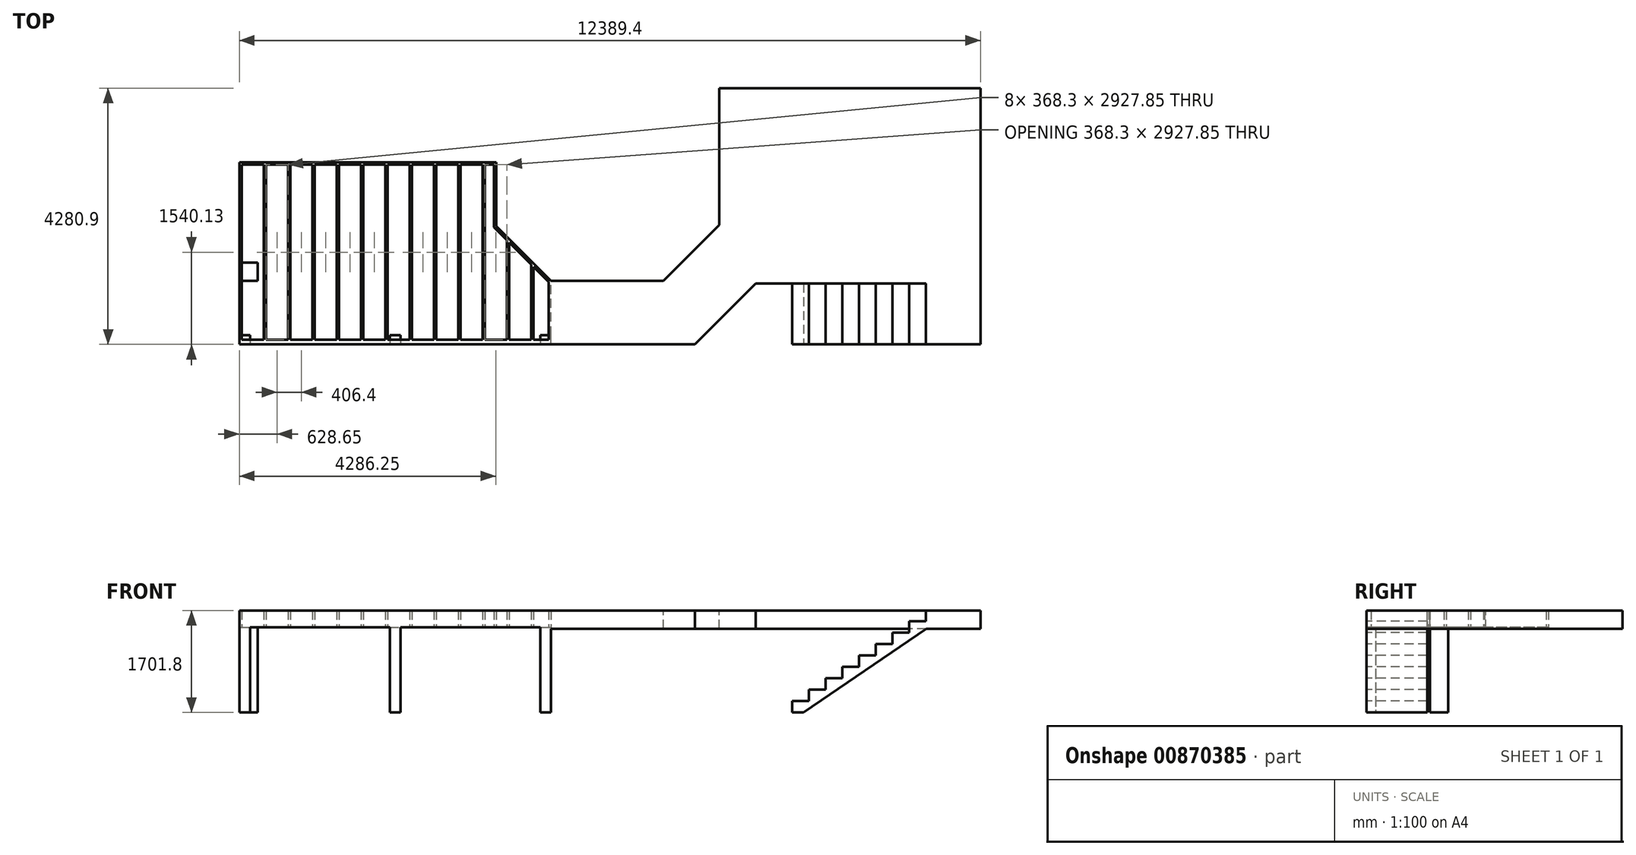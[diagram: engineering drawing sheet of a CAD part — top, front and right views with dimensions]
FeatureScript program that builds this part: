
annotation { "Feature Type Name" : "Feature", "Feature Type Description" : "" }
export const myFeature = defineFeature(function(context is Context, id is Id, definition is map)
    precondition{}
    {
        {
            var Q0;
            Q0=qCreatedBy(makeId("Top.planeOp"),FACE);
            var sketch = newSketch(context, id + "F0", { "sketchPlane" : qUnion([Q0])});
            skLineSegment(sketch, "E0.bottom", {"start": v(0, -1676.4) * mm, "end": v(304.8, -1676.4) * mm});
            skLineSegment(sketch, "E0.top", {"start": v(0, -1981.2) * mm, "end": v(304.8, -1981.2) * mm});
            skLineSegment(sketch, "E0.left", {"start": v(0, -1676.4) * mm, "end": v(0, -1981.2) * mm});
            skLineSegment(sketch, "E0.right", {"start": v(304.8, -1676.4) * mm, "end": v(304.8, -1981.2) * mm});
            skLineSegment(sketch, "E1.bottom", {"start": v(0, -2889.75) * mm, "end": v(177.8, -2889.75) * mm});
            skLineSegment(sketch, "E1.top", {"start": v(0, -3042.15) * mm, "end": v(177.8, -3042.15) * mm});
            skLineSegment(sketch, "E1.left", {"start": v(0, -2889.75) * mm, "end": v(0, -3042.15) * mm});
            skLineSegment(sketch, "E1.right", {"start": v(177.8, -2889.75) * mm, "end": v(177.8, -3042.15) * mm});
            skLineSegment(sketch, "E2.bottom", {"start": v(2514.6, -2889.75) * mm, "end": v(2692.4, -2889.75) * mm});
            skLineSegment(sketch, "E2.top", {"start": v(2514.6, -3042.15) * mm, "end": v(2692.4, -3042.15) * mm});
            skLineSegment(sketch, "E2.left", {"start": v(2514.6, -2889.75) * mm, "end": v(2514.6, -3042.15) * mm});
            skLineSegment(sketch, "E2.right", {"start": v(2692.4, -2889.75) * mm, "end": v(2692.4, -3042.15) * mm});
            skLineSegment(sketch, "E3.bottom", {"start": v(5029.2, -2889.75) * mm, "end": v(5207, -2889.75) * mm});
            skLineSegment(sketch, "E3.top", {"start": v(5029.2, -3042.15) * mm, "end": v(5207, -3042.15) * mm});
            skLineSegment(sketch, "E3.left", {"start": v(5029.2, -2889.75) * mm, "end": v(5029.2, -3042.15) * mm});
            skLineSegment(sketch, "E3.right", {"start": v(5207, -2889.75) * mm, "end": v(5207, -3042.15) * mm});
            skLineSegment(sketch, "E4", {"start": v(0, 0) * mm, "end": v(4292.6, 0) * mm, "construction": true});
            skLineSegment(sketch, "E5", {"start": v(4292.6, 0) * mm, "end": v(4292.6, -1066.8) * mm, "construction": true});
            skLineSegment(sketch, "E6", {"start": v(4292.6, -1066.8) * mm, "end": v(5226.55, -2000.75) * mm, "construction": true});
            skLineSegment(sketch, "E7", {"start": v(5226.55, -2000.75) * mm, "end": v(7106.15, -2000.75) * mm, "construction": true});
            skSolve(sketch);
        }
        {
            var Q0;
            Q0=qSketchRegion(id+"F0",true);
            extrude(context, id + "F1", {"entities" : qUnion([Q0]), "depth" : 1422.4 * mm, "offsetDistance" : 25.4 * mm});
        }
        {
            var Q0;
            Q0=makeQuery(id+"F1.opExtrude","CAP_FACE",FACE,{"disambiguationData":[OSD([sQuery(id+"F0.wireOp",EDGE,"E0.bottom"),sQuery(id+"F0.wireOp",EDGE,"E0.top"),sQuery(id+"F0.wireOp",EDGE,"E0.left"),sQuery(id+"F0.wireOp",EDGE,"E0.right")])],"isStart":false});
            var sketch = newSketch(context, id + "F2", { "sketchPlane" : qUnion([Q0])});
            skLineSegment(sketch, "E8.0", {"start": v(0, 0) * mm, "end": v(4292.6, 0) * mm});
            skLineSegment(sketch, "E9.0", {"start": v(4292.6, 0) * mm, "end": v(4292.6, -1066.8) * mm});
            skLineSegment(sketch, "E9.1", {"start": v(4292.6, -1066.8) * mm, "end": v(5207, -1981.2) * mm});
            skLineSegment(sketch, "E10", {"start": v(0, 0) * mm, "end": v(0, -3042.15) * mm});
            skLineSegment(sketch, "E11", {"start": v(0, -3042.15) * mm, "end": v(5207, -3042.15) * mm});
            skLineSegment(sketch, "E12", {"start": v(5207, -3042.15) * mm, "end": v(5207, -1981.2) * mm});
            skPoint(sketch, "E13.orphan", {"position": v(5226.55, -2000.75) * mm});
            skLineSegment(sketch, "E14.0", {"start": v(4254.5, -38.1) * mm, "end": v(4254.5, -1082.58) * mm});
            skLineSegment(sketch, "E14.1", {"start": v(5168.9, -3004.05) * mm, "end": v(5168.9, -1996.98) * mm});
            skLineSegment(sketch, "E14.2", {"start": v(38.1, -3004.05) * mm, "end": v(5168.9, -3004.05) * mm});
            skLineSegment(sketch, "E14.3", {"start": v(4254.5, -1082.58) * mm, "end": v(5168.9, -1996.98) * mm});
            skLineSegment(sketch, "E14.4", {"start": v(38.1, -38.1) * mm, "end": v(38.1, -3004.05) * mm});
            skLineSegment(sketch, "E14.5", {"start": v(38.1, -38.1) * mm, "end": v(4254.5, -38.1) * mm});
            skSolve(sketch);
        }
        {
            var Q0;
            Q0=qSketchRegion(id+"F2",true);
            extrude(context, id + "F3", {"entities" : qUnion([Q0]), "operationType" : NewBodyOperationType.ADD, "depth" : 279.4 * mm, "offsetDistance" : 25.4 * mm});
        }
        {
            var Q0;
            Q0=makeQuery(id+"F1.opExtrude","CAP_FACE",FACE,{"disambiguationData":[OSD([sQuery(id+"F0.wireOp",EDGE,"E1.bottom"),sQuery(id+"F0.wireOp",EDGE,"E1.top"),sQuery(id+"F0.wireOp",EDGE,"E1.left"),sQuery(id+"F0.wireOp",EDGE,"E1.right")])],"isStart":false});
            var sketch = newSketch(context, id + "F4", { "sketchPlane" : qUnion([Q0])});
            skPoint(sketch, "E15.oppositeSnap0", {"position": v(38.1, -2965.95) * mm});
            skLineSegment(sketch, "E15.bottom", {"start": v(38.1, -3004.05) * mm, "end": v(5168.9, -3004.05) * mm});
            skLineSegment(sketch, "E15.top", {"start": v(38.1, -2965.95) * mm, "end": v(5168.9, -2965.95) * mm});
            skLineSegment(sketch, "E15.left", {"start": v(38.1, -3004.05) * mm, "end": v(38.1, -2965.95) * mm});
            skLineSegment(sketch, "E15.right", {"start": v(5168.9, -3004.05) * mm, "end": v(5168.9, -2965.95) * mm});
            skSolve(sketch);
        }
        {
            var Q0;
            Q0=qSketchRegion(id+"F4",true);
            var Q1;
            Q1=makeQuery(id+"F3.opExtrude","CAP_FACE",FACE,{"disambiguationData":[OSD([sQuery(id+"F2.wireOp",EDGE,"E8.0"),sQuery(id+"F2.wireOp",EDGE,"E9.0"),sQuery(id+"F2.wireOp",EDGE,"E9.1"),sQuery(id+"F2.wireOp",EDGE,"E10"),sQuery(id+"F2.wireOp",EDGE,"E11"),sQuery(id+"F2.wireOp",EDGE,"E12"),sQuery(id+"F2.wireOp",EDGE,"E14.0"),sQuery(id+"F2.wireOp",EDGE,"E14.1"),sQuery(id+"F2.wireOp",EDGE,"E14.2"),sQuery(id+"F2.wireOp",EDGE,"E14.3"),sQuery(id+"F2.wireOp",EDGE,"E14.4"),sQuery(id+"F2.wireOp",EDGE,"E14.5")])],"isStart":false});
            extrude(context, id + "F5", {"entities" : qUnion([Q0]), "operationType" : NewBodyOperationType.ADD, "endBound" : BoundingType.UP_TO_SURFACE, "depth" : 25.4 * mm, "endBoundEntityFace" : qUnion([Q1]), "offsetDistance" : 25.4 * mm});
        }
        {
            var Q0;
            Q0=makeQuery(id+"F1.opExtrude","CAP_FACE",FACE,{"disambiguationData":[OSD([sQuery(id+"F0.wireOp",EDGE,"E0.bottom"),sQuery(id+"F0.wireOp",EDGE,"E0.top"),sQuery(id+"F0.wireOp",EDGE,"E0.left"),sQuery(id+"F0.wireOp",EDGE,"E0.right")])],"isStart":false});
            var sketch = newSketch(context, id + "F6", { "sketchPlane" : qUnion([Q0])});
            skLineSegment(sketch, "E16.bottom", {"start": v(406.4, -38.1) * mm, "end": v(444.5, -38.1) * mm});
            skLineSegment(sketch, "E16.top", {"start": v(406.4, -2965.95) * mm, "end": v(444.5, -2965.95) * mm});
            skLineSegment(sketch, "E16.left", {"start": v(406.4, -38.1) * mm, "end": v(406.4, -2965.95) * mm});
            skLineSegment(sketch, "E16.right", {"start": v(444.5, -38.1) * mm, "end": v(444.5, -2965.95) * mm});
            skLineSegment(sketch, "E17.1.0.0", {"start": v(850.9, -38.1) * mm, "end": v(850.9, -2965.95) * mm});
            skLineSegment(sketch, "E17.1.0.1", {"start": v(812.8, -38.1) * mm, "end": v(812.8, -2965.95) * mm});
            skLineSegment(sketch, "E17.1.0.2", {"start": v(812.8, -38.1) * mm, "end": v(850.9, -38.1) * mm});
            skLineSegment(sketch, "E17.1.0.3", {"start": v(812.8, -2965.95) * mm, "end": v(850.9, -2965.95) * mm});
            skLineSegment(sketch, "E17.2.0.0", {"start": v(1257.3, -38.1) * mm, "end": v(1257.3, -2965.95) * mm});
            skLineSegment(sketch, "E17.2.0.1", {"start": v(1219.2, -38.1) * mm, "end": v(1219.2, -2965.95) * mm});
            skLineSegment(sketch, "E17.2.0.2", {"start": v(1219.2, -38.1) * mm, "end": v(1257.3, -38.1) * mm});
            skLineSegment(sketch, "E17.2.0.3", {"start": v(1219.2, -2965.95) * mm, "end": v(1257.3, -2965.95) * mm});
            skLineSegment(sketch, "E17.3.0.0", {"start": v(1663.7, -38.1) * mm, "end": v(1663.7, -2965.95) * mm});
            skLineSegment(sketch, "E17.3.0.1", {"start": v(1625.6, -38.1) * mm, "end": v(1625.6, -2965.95) * mm});
            skLineSegment(sketch, "E17.3.0.2", {"start": v(1625.6, -38.1) * mm, "end": v(1663.7, -38.1) * mm});
            skLineSegment(sketch, "E17.3.0.3", {"start": v(1625.6, -2965.95) * mm, "end": v(1663.7, -2965.95) * mm});
            skLineSegment(sketch, "E17.4.0.0", {"start": v(2070.1, -38.1) * mm, "end": v(2070.1, -2965.95) * mm});
            skLineSegment(sketch, "E17.4.0.1", {"start": v(2032, -38.1) * mm, "end": v(2032, -2965.95) * mm});
            skLineSegment(sketch, "E17.4.0.2", {"start": v(2032, -38.1) * mm, "end": v(2070.1, -38.1) * mm});
            skLineSegment(sketch, "E17.4.0.3", {"start": v(2032, -2965.95) * mm, "end": v(2070.1, -2965.95) * mm});
            skLineSegment(sketch, "E17.5.0.0", {"start": v(2476.5, -38.1) * mm, "end": v(2476.5, -2965.95) * mm});
            skLineSegment(sketch, "E17.5.0.1", {"start": v(2438.4, -38.1) * mm, "end": v(2438.4, -2965.95) * mm});
            skLineSegment(sketch, "E17.5.0.2", {"start": v(2438.4, -38.1) * mm, "end": v(2476.5, -38.1) * mm});
            skLineSegment(sketch, "E17.5.0.3", {"start": v(2438.4, -2965.95) * mm, "end": v(2476.5, -2965.95) * mm});
            skLineSegment(sketch, "E17.6.0.0", {"start": v(2882.9, -38.1) * mm, "end": v(2882.9, -2965.95) * mm});
            skLineSegment(sketch, "E17.6.0.1", {"start": v(2844.8, -38.1) * mm, "end": v(2844.8, -2965.95) * mm});
            skLineSegment(sketch, "E17.6.0.2", {"start": v(2844.8, -38.1) * mm, "end": v(2882.9, -38.1) * mm});
            skLineSegment(sketch, "E17.6.0.3", {"start": v(2844.8, -2965.95) * mm, "end": v(2882.9, -2965.95) * mm});
            skLineSegment(sketch, "E17.7.0.0", {"start": v(3289.3, -38.1) * mm, "end": v(3289.3, -2965.95) * mm});
            skLineSegment(sketch, "E17.7.0.1", {"start": v(3251.2, -38.1) * mm, "end": v(3251.2, -2965.95) * mm});
            skLineSegment(sketch, "E17.7.0.2", {"start": v(3251.2, -38.1) * mm, "end": v(3289.3, -38.1) * mm});
            skLineSegment(sketch, "E17.7.0.3", {"start": v(3251.2, -2965.95) * mm, "end": v(3289.3, -2965.95) * mm});
            skLineSegment(sketch, "E17.8.0.0", {"start": v(3695.7, -38.1) * mm, "end": v(3695.7, -2965.95) * mm});
            skLineSegment(sketch, "E17.8.0.1", {"start": v(3657.6, -38.1) * mm, "end": v(3657.6, -2965.95) * mm});
            skLineSegment(sketch, "E17.8.0.2", {"start": v(3657.6, -38.1) * mm, "end": v(3695.7, -38.1) * mm});
            skLineSegment(sketch, "E17.8.0.3", {"start": v(3657.6, -2965.95) * mm, "end": v(3695.7, -2965.95) * mm});
            skLineSegment(sketch, "E17.9.0.0", {"start": v(4102.1, -38.1) * mm, "end": v(4102.1, -2965.95) * mm});
            skLineSegment(sketch, "E17.9.0.1", {"start": v(4064, -38.1) * mm, "end": v(4064, -2965.95) * mm});
            skLineSegment(sketch, "E17.9.0.2", {"start": v(4064, -38.1) * mm, "end": v(4102.1, -38.1) * mm});
            skLineSegment(sketch, "E17.9.0.3", {"start": v(4064, -2965.95) * mm, "end": v(4102.1, -2965.95) * mm});
            skLineSegment(sketch, "E17.direction1", {"start": v(406.4, -2965.95) * mm, "end": v(812.8, -2965.95) * mm, "construction": true});
            skLineSegment(sketch, "E18.top", {"start": v(4470.4, -2965.95) * mm, "end": v(4508.5, -2965.95) * mm});
            skLineSegment(sketch, "E18.left", {"start": v(4470.4, -1298.48) * mm, "end": v(4470.4, -2965.95) * mm});
            skLineSegment(sketch, "E18.right", {"start": v(4508.5, -1336.58) * mm, "end": v(4508.5, -2965.95) * mm});
            skLineSegment(sketch, "E19.top", {"start": v(4876.8, -2965.95) * mm, "end": v(4914.9, -2965.95) * mm});
            skLineSegment(sketch, "E19.left", {"start": v(4876.8, -1704.88) * mm, "end": v(4876.8, -2965.95) * mm});
            skLineSegment(sketch, "E19.right", {"start": v(4914.9, -1742.98) * mm, "end": v(4914.9, -2965.95) * mm});
            skLineSegment(sketch, "E20", {"start": v(4470.4, -1298.48) * mm, "end": v(4508.5, -1336.58) * mm});
            skLineSegment(sketch, "E21.trimOffspring", {"start": v(4876.8, -1704.88) * mm, "end": v(4914.9, -1742.98) * mm});
            skSolve(sketch);
        }
        {
            var Q0;
            Q0=qSketchRegion(id+"F6",true);
            var Q1;
            {var subQ0=sQuery(id+"F2.wireOp",EDGE,"E14.5");var subQ1=sQuery(id+"F2.wireOp",EDGE,"E14.4");var subQ2=sQuery(id+"F2.wireOp",EDGE,"E14.3");var subQ3=sQuery(id+"F2.wireOp",EDGE,"E14.2");var subQ4=sQuery(id+"F2.wireOp",EDGE,"E14.1");var subQ5=sQuery(id+"F2.wireOp",EDGE,"E14.0");var subQ6=sQuery(id+"F2.wireOp",EDGE,"E12");var subQ7=sQuery(id+"F2.wireOp",EDGE,"E11");var subQ8=sQuery(id+"F2.wireOp",EDGE,"E10");var subQ9=sQuery(id+"F2.wireOp",EDGE,"E9.1");var subQ10=sQuery(id+"F2.wireOp",EDGE,"E9.0");var subQ11=sQuery(id+"F2.wireOp",EDGE,"E8.0");Q1=makeQuery(id+"F5.boolean.opBoolean","MERGE",FACE,{"derivedFrom":[makeQuery(id+"F3.opExtrude","CAP_FACE",FACE,{"disambiguationData":[OSD([subQ11,subQ10,subQ9,subQ8,subQ7,subQ6,subQ5,subQ4,subQ3,subQ2,subQ1,subQ0])],"isStart":false}),makeQuery(id+"F5.opExtrude","CAP_FACE",FACE,{"disambiguationData":[OSD([subQ11,subQ10,subQ9,subQ8,subQ7,subQ6,subQ5,subQ4,subQ3,subQ2,subQ1,subQ0])],"isStart":false})]});}
            extrude(context, id + "F7", {"entities" : qUnion([Q0]), "operationType" : NewBodyOperationType.ADD, "endBound" : BoundingType.UP_TO_SURFACE, "depth" : 25.4 * mm, "endBoundEntityFace" : qUnion([Q1]), "offsetDistance" : 25.4 * mm});
        }
        {
            var Q0;
            Q0=makeQuery(id+"F7.boolean.opBoolean","MERGE",FACE,{"derivedFrom":[makeQuery(id+"F5.boolean.opBoolean","MERGE",FACE,{"derivedFrom":[makeQuery(id+"F3.opExtrude","CAP_FACE",FACE,{"disambiguationData":[OSD([sQuery(id+"F2.wireOp",EDGE,"E8.0"),sQuery(id+"F2.wireOp",EDGE,"E9.0"),sQuery(id+"F2.wireOp",EDGE,"E9.1"),sQuery(id+"F2.wireOp",EDGE,"E10"),sQuery(id+"F2.wireOp",EDGE,"E11"),sQuery(id+"F2.wireOp",EDGE,"E12"),sQuery(id+"F2.wireOp",EDGE,"E14.0"),sQuery(id+"F2.wireOp",EDGE,"E14.1"),sQuery(id+"F2.wireOp",EDGE,"E14.2"),sQuery(id+"F2.wireOp",EDGE,"E14.3"),sQuery(id+"F2.wireOp",EDGE,"E14.4"),sQuery(id+"F2.wireOp",EDGE,"E14.5")])],"isStart":false}),makeQuery(id+"F5.opExtrude","CAP_FACE",FACE,{"disambiguationData":[OSD([sQuery(id+"F4.wireOp",EDGE,"E15.bottom"),sQuery(id+"F4.wireOp",EDGE,"E15.top"),sQuery(id+"F4.wireOp",EDGE,"E15.left"),sQuery(id+"F4.wireOp",EDGE,"E15.right")])],"isStart":false})]}),makeQuery(id+"F7.opExtrude","CAP_FACE",FACE,{"disambiguationData":[OSD([sQuery(id+"F6.wireOp",EDGE,"E16.bottom"),sQuery(id+"F6.wireOp",EDGE,"E16.top"),sQuery(id+"F6.wireOp",EDGE,"E16.left"),sQuery(id+"F6.wireOp",EDGE,"E16.right")])],"isStart":false}),makeQuery(id+"F7.opExtrude","CAP_FACE",FACE,{"disambiguationData":[OSD([sQuery(id+"F6.wireOp",EDGE,"E17.1.0.0"),sQuery(id+"F6.wireOp",EDGE,"E17.1.0.1"),sQuery(id+"F6.wireOp",EDGE,"E17.1.0.2"),sQuery(id+"F6.wireOp",EDGE,"E17.1.0.3")])],"isStart":false}),makeQuery(id+"F7.opExtrude","CAP_FACE",FACE,{"disambiguationData":[OSD([sQuery(id+"F6.wireOp",EDGE,"E17.2.0.0"),sQuery(id+"F6.wireOp",EDGE,"E17.2.0.1"),sQuery(id+"F6.wireOp",EDGE,"E17.2.0.2"),sQuery(id+"F6.wireOp",EDGE,"E17.2.0.3")])],"isStart":false}),makeQuery(id+"F7.opExtrude","CAP_FACE",FACE,{"disambiguationData":[OSD([sQuery(id+"F6.wireOp",EDGE,"E17.3.0.0"),sQuery(id+"F6.wireOp",EDGE,"E17.3.0.1"),sQuery(id+"F6.wireOp",EDGE,"E17.3.0.2"),sQuery(id+"F6.wireOp",EDGE,"E17.3.0.3")])],"isStart":false}),makeQuery(id+"F7.opExtrude","CAP_FACE",FACE,{"disambiguationData":[OSD([sQuery(id+"F6.wireOp",EDGE,"E17.4.0.0"),sQuery(id+"F6.wireOp",EDGE,"E17.4.0.1"),sQuery(id+"F6.wireOp",EDGE,"E17.4.0.2"),sQuery(id+"F6.wireOp",EDGE,"E17.4.0.3")])],"isStart":false}),makeQuery(id+"F7.opExtrude","CAP_FACE",FACE,{"disambiguationData":[OSD([sQuery(id+"F6.wireOp",EDGE,"E17.5.0.0"),sQuery(id+"F6.wireOp",EDGE,"E17.5.0.1"),sQuery(id+"F6.wireOp",EDGE,"E17.5.0.2"),sQuery(id+"F6.wireOp",EDGE,"E17.5.0.3")])],"isStart":false}),makeQuery(id+"F7.opExtrude","CAP_FACE",FACE,{"disambiguationData":[OSD([sQuery(id+"F6.wireOp",EDGE,"E17.6.0.0"),sQuery(id+"F6.wireOp",EDGE,"E17.6.0.1"),sQuery(id+"F6.wireOp",EDGE,"E17.6.0.2"),sQuery(id+"F6.wireOp",EDGE,"E17.6.0.3")])],"isStart":false}),makeQuery(id+"F7.opExtrude","CAP_FACE",FACE,{"disambiguationData":[OSD([sQuery(id+"F6.wireOp",EDGE,"E17.7.0.0"),sQuery(id+"F6.wireOp",EDGE,"E17.7.0.1"),sQuery(id+"F6.wireOp",EDGE,"E17.7.0.2"),sQuery(id+"F6.wireOp",EDGE,"E17.7.0.3")])],"isStart":false}),makeQuery(id+"F7.opExtrude","CAP_FACE",FACE,{"disambiguationData":[OSD([sQuery(id+"F6.wireOp",EDGE,"E17.8.0.0"),sQuery(id+"F6.wireOp",EDGE,"E17.8.0.1"),sQuery(id+"F6.wireOp",EDGE,"E17.8.0.2"),sQuery(id+"F6.wireOp",EDGE,"E17.8.0.3")])],"isStart":false}),makeQuery(id+"F7.opExtrude","CAP_FACE",FACE,{"disambiguationData":[OSD([sQuery(id+"F6.wireOp",EDGE,"E17.9.0.0"),sQuery(id+"F6.wireOp",EDGE,"E17.9.0.1"),sQuery(id+"F6.wireOp",EDGE,"E17.9.0.2"),sQuery(id+"F6.wireOp",EDGE,"E17.9.0.3")])],"isStart":false}),makeQuery(id+"F7.opExtrude","CAP_FACE",FACE,{"disambiguationData":[OSD([sQuery(id+"F6.wireOp",EDGE,"E18.top"),sQuery(id+"F6.wireOp",EDGE,"E18.left"),sQuery(id+"F6.wireOp",EDGE,"E18.right"),sQuery(id+"F6.wireOp",EDGE,"E20")])],"isStart":false}),makeQuery(id+"F7.opExtrude","CAP_FACE",FACE,{"disambiguationData":[OSD([sQuery(id+"F6.wireOp",EDGE,"E19.top"),sQuery(id+"F6.wireOp",EDGE,"E19.left"),sQuery(id+"F6.wireOp",EDGE,"E19.right"),sQuery(id+"F6.wireOp",EDGE,"E21.trimOffspring")])],"isStart":false})]});
            var sketch = newSketch(context, id + "F8", { "sketchPlane" : qUnion([Q0])});
            skLineSegment(sketch, "E22", {"start": v(5207, -1981.2) * mm, "end": v(5207, -3042.15) * mm});
            skLineSegment(sketch, "E23", {"start": v(5207, -1981.2) * mm, "end": v(7086.6, -1981.2) * mm});
            skLineSegment(sketch, "E24", {"start": v(7086.6, -1981.2) * mm, "end": v(8020.55, -1047.25) * mm});
            skLineSegment(sketch, "E25", {"start": v(8020.55, -1047.25) * mm, "end": v(8020.55, 1238.75) * mm});
            skLineSegment(sketch, "E26", {"start": v(8020.55, 1238.75) * mm, "end": v(12389.35, 1238.75) * mm});
            skLineSegment(sketch, "E27", {"start": v(12389.35, 1238.75) * mm, "end": v(12389.35, -3042.15) * mm});
            skLineSegment(sketch, "E28", {"start": v(5207, -3042.15) * mm, "end": v(12389.35, -3042.15) * mm});
            skSolve(sketch);
        }
        {
            var Q0;
            Q0=qSketchRegion(id+"F8",true);
            extrude(context, id + "F9", {"entities" : qUnion([Q0]), "operationType" : NewBodyOperationType.ADD, "oppositeDirection" : true, "depth" : 304.8 * mm, "offsetDistance" : 25.4 * mm});
        }
        {
            var Q0;
            Q0=makeQuery(id+"F9.boolean.opBoolean","MERGE",FACE,{"derivedFrom":[makeQuery(id+"F7.boolean.opBoolean","MERGE",FACE,{"derivedFrom":[makeQuery(id+"F5.boolean.opBoolean","MERGE",FACE,{"derivedFrom":[makeQuery(id+"F3.opExtrude","CAP_FACE",FACE,{"disambiguationData":[OSD([sQuery(id+"F2.wireOp",EDGE,"E8.0"),sQuery(id+"F2.wireOp",EDGE,"E9.0"),sQuery(id+"F2.wireOp",EDGE,"E9.1"),sQuery(id+"F2.wireOp",EDGE,"E10"),sQuery(id+"F2.wireOp",EDGE,"E11"),sQuery(id+"F2.wireOp",EDGE,"E12"),sQuery(id+"F2.wireOp",EDGE,"E14.0"),sQuery(id+"F2.wireOp",EDGE,"E14.1"),sQuery(id+"F2.wireOp",EDGE,"E14.2"),sQuery(id+"F2.wireOp",EDGE,"E14.3"),sQuery(id+"F2.wireOp",EDGE,"E14.4"),sQuery(id+"F2.wireOp",EDGE,"E14.5")])],"isStart":false}),makeQuery(id+"F5.opExtrude","CAP_FACE",FACE,{"disambiguationData":[OSD([sQuery(id+"F4.wireOp",EDGE,"E15.bottom"),sQuery(id+"F4.wireOp",EDGE,"E15.top"),sQuery(id+"F4.wireOp",EDGE,"E15.left"),sQuery(id+"F4.wireOp",EDGE,"E15.right")])],"isStart":false})]}),makeQuery(id+"F7.opExtrude","CAP_FACE",FACE,{"disambiguationData":[OSD([sQuery(id+"F6.wireOp",EDGE,"E16.bottom"),sQuery(id+"F6.wireOp",EDGE,"E16.top"),sQuery(id+"F6.wireOp",EDGE,"E16.left"),sQuery(id+"F6.wireOp",EDGE,"E16.right")])],"isStart":false}),makeQuery(id+"F7.opExtrude","CAP_FACE",FACE,{"disambiguationData":[OSD([sQuery(id+"F6.wireOp",EDGE,"E17.1.0.0"),sQuery(id+"F6.wireOp",EDGE,"E17.1.0.1"),sQuery(id+"F6.wireOp",EDGE,"E17.1.0.2"),sQuery(id+"F6.wireOp",EDGE,"E17.1.0.3")])],"isStart":false}),makeQuery(id+"F7.opExtrude","CAP_FACE",FACE,{"disambiguationData":[OSD([sQuery(id+"F6.wireOp",EDGE,"E17.2.0.0"),sQuery(id+"F6.wireOp",EDGE,"E17.2.0.1"),sQuery(id+"F6.wireOp",EDGE,"E17.2.0.2"),sQuery(id+"F6.wireOp",EDGE,"E17.2.0.3")])],"isStart":false}),makeQuery(id+"F7.opExtrude","CAP_FACE",FACE,{"disambiguationData":[OSD([sQuery(id+"F6.wireOp",EDGE,"E17.3.0.0"),sQuery(id+"F6.wireOp",EDGE,"E17.3.0.1"),sQuery(id+"F6.wireOp",EDGE,"E17.3.0.2"),sQuery(id+"F6.wireOp",EDGE,"E17.3.0.3")])],"isStart":false}),makeQuery(id+"F7.opExtrude","CAP_FACE",FACE,{"disambiguationData":[OSD([sQuery(id+"F6.wireOp",EDGE,"E17.4.0.0"),sQuery(id+"F6.wireOp",EDGE,"E17.4.0.1"),sQuery(id+"F6.wireOp",EDGE,"E17.4.0.2"),sQuery(id+"F6.wireOp",EDGE,"E17.4.0.3")])],"isStart":false}),makeQuery(id+"F7.opExtrude","CAP_FACE",FACE,{"disambiguationData":[OSD([sQuery(id+"F6.wireOp",EDGE,"E17.5.0.0"),sQuery(id+"F6.wireOp",EDGE,"E17.5.0.1"),sQuery(id+"F6.wireOp",EDGE,"E17.5.0.2"),sQuery(id+"F6.wireOp",EDGE,"E17.5.0.3")])],"isStart":false}),makeQuery(id+"F7.opExtrude","CAP_FACE",FACE,{"disambiguationData":[OSD([sQuery(id+"F6.wireOp",EDGE,"E17.6.0.0"),sQuery(id+"F6.wireOp",EDGE,"E17.6.0.1"),sQuery(id+"F6.wireOp",EDGE,"E17.6.0.2"),sQuery(id+"F6.wireOp",EDGE,"E17.6.0.3")])],"isStart":false}),makeQuery(id+"F7.opExtrude","CAP_FACE",FACE,{"disambiguationData":[OSD([sQuery(id+"F6.wireOp",EDGE,"E17.7.0.0"),sQuery(id+"F6.wireOp",EDGE,"E17.7.0.1"),sQuery(id+"F6.wireOp",EDGE,"E17.7.0.2"),sQuery(id+"F6.wireOp",EDGE,"E17.7.0.3")])],"isStart":false}),makeQuery(id+"F7.opExtrude","CAP_FACE",FACE,{"disambiguationData":[OSD([sQuery(id+"F6.wireOp",EDGE,"E17.8.0.0"),sQuery(id+"F6.wireOp",EDGE,"E17.8.0.1"),sQuery(id+"F6.wireOp",EDGE,"E17.8.0.2"),sQuery(id+"F6.wireOp",EDGE,"E17.8.0.3")])],"isStart":false}),makeQuery(id+"F7.opExtrude","CAP_FACE",FACE,{"disambiguationData":[OSD([sQuery(id+"F6.wireOp",EDGE,"E17.9.0.0"),sQuery(id+"F6.wireOp",EDGE,"E17.9.0.1"),sQuery(id+"F6.wireOp",EDGE,"E17.9.0.2"),sQuery(id+"F6.wireOp",EDGE,"E17.9.0.3")])],"isStart":false}),makeQuery(id+"F7.opExtrude","CAP_FACE",FACE,{"disambiguationData":[OSD([sQuery(id+"F6.wireOp",EDGE,"E18.top"),sQuery(id+"F6.wireOp",EDGE,"E18.left"),sQuery(id+"F6.wireOp",EDGE,"E18.right"),sQuery(id+"F6.wireOp",EDGE,"E20")])],"isStart":false}),makeQuery(id+"F7.opExtrude","CAP_FACE",FACE,{"disambiguationData":[OSD([sQuery(id+"F6.wireOp",EDGE,"E19.top"),sQuery(id+"F6.wireOp",EDGE,"E19.left"),sQuery(id+"F6.wireOp",EDGE,"E19.right"),sQuery(id+"F6.wireOp",EDGE,"E21.trimOffspring")])],"isStart":false})]}),makeQuery(id+"F9.opExtrude","CAP_FACE",FACE,{"disambiguationData":[OSD([sQuery(id+"F8.wireOp",EDGE,"E22"),sQuery(id+"F8.wireOp",EDGE,"E23"),sQuery(id+"F8.wireOp",EDGE,"E24"),sQuery(id+"F8.wireOp",EDGE,"E25"),sQuery(id+"F8.wireOp",EDGE,"E26"),sQuery(id+"F8.wireOp",EDGE,"E27"),sQuery(id+"F8.wireOp",EDGE,"E28")])],"isStart":true})]});
            var sketch = newSketch(context, id + "F10", { "sketchPlane" : qUnion([Q0])});
            skLineSegment(sketch, "E29.bottom", {"start": v(11474.95, -3042.15) * mm, "end": v(9239.75, -3042.15) * mm});
            skLineSegment(sketch, "E29.top", {"start": v(11474.95, -2026.15) * mm, "end": v(9239.75, -2026.15) * mm});
            skLineSegment(sketch, "E29.left", {"start": v(11474.95, -3042.15) * mm, "end": v(11474.95, -2026.15) * mm});
            skLineSegment(sketch, "E29.right", {"start": v(9239.75, -3042.15) * mm, "end": v(9239.75, -2026.15) * mm});
            skSolve(sketch);
        }
        {
            var Q0;
            Q0=qSketchRegion(id+"F10",true);
            extrude(context, id + "F11", {"entities" : qUnion([Q0]), "operationType" : NewBodyOperationType.REMOVE, "endBound" : BoundingType.THROUGH_ALL, "oppositeDirection" : true, "depth" : 25.4 * mm, "offsetDistance" : 25.4 * mm});
        }
        {
            var Q0;
            Q0=makeQuery(id+"F9.boolean.opBoolean","MERGE",FACE,{"derivedFrom":[makeQuery(id+"F3.boolean.opBoolean","MERGE",FACE,{"derivedFrom":[makeQuery(id+"F1.opExtrude","SWEPT_FACE",FACE,{"disambiguationData":[OSD([sQuery(id+"F0.wireOp",EDGE,"E1.top")])]}),makeQuery(id+"F1.opExtrude","SWEPT_FACE",FACE,{"disambiguationData":[OSD([sQuery(id+"F0.wireOp",EDGE,"E2.top")])]}),makeQuery(id+"F1.opExtrude","SWEPT_FACE",FACE,{"disambiguationData":[OSD([sQuery(id+"F0.wireOp",EDGE,"E3.top")])]}),makeQuery(id+"F3.opExtrude","SWEPT_FACE",FACE,{"disambiguationData":[OSD([sQuery(id+"F2.wireOp",EDGE,"E11")])]})]}),makeQuery(id+"F9.opExtrude","SWEPT_FACE",FACE,{"disambiguationData":[OSD([sQuery(id+"F8.wireOp",EDGE,"E28")])]})]});
            var sketch = newSketch(context, id + "F12", { "sketchPlane" : qUnion([Q0])});
            skLineSegment(sketch, "E30", {"start": v(11195.55, 1524) * mm, "end": v(11474.95, 1524) * mm});
            skLineSegment(sketch, "E31", {"start": v(11195.55, 1524) * mm, "end": v(11195.55, 1333.5) * mm});
            skLineSegment(sketch, "E32", {"start": v(10916.15, 1333.5) * mm, "end": v(11195.55, 1333.5) * mm});
            skLineSegment(sketch, "E33", {"start": v(10916.15, 1333.5) * mm, "end": v(10916.15, 1143) * mm});
            skLineSegment(sketch, "E34", {"start": v(10636.75, 1143) * mm, "end": v(10916.15, 1143) * mm});
            skLineSegment(sketch, "E35", {"start": v(10636.75, 1143) * mm, "end": v(10636.75, 952.5) * mm});
            skLineSegment(sketch, "E36", {"start": v(10357.35, 952.5) * mm, "end": v(10636.75, 952.5) * mm});
            skLineSegment(sketch, "E37", {"start": v(10357.35, 952.5) * mm, "end": v(10357.35, 762) * mm});
            skLineSegment(sketch, "E38", {"start": v(10077.95, 762) * mm, "end": v(10357.35, 762) * mm});
            skLineSegment(sketch, "E39", {"start": v(10077.95, 762) * mm, "end": v(10077.95, 571.5) * mm});
            skLineSegment(sketch, "E40", {"start": v(9798.55, 571.5) * mm, "end": v(10077.95, 571.5) * mm});
            skLineSegment(sketch, "E41", {"start": v(9798.55, 571.5) * mm, "end": v(9798.55, 381) * mm});
            skLineSegment(sketch, "E42", {"start": v(9519.15, 381) * mm, "end": v(9798.55, 381) * mm});
            skLineSegment(sketch, "E43", {"start": v(9519.15, 381) * mm, "end": v(9519.15, 190.5) * mm});
            skLineSegment(sketch, "E44", {"start": v(9239.75, 190.5) * mm, "end": v(9519.15, 190.5) * mm});
            skLineSegment(sketch, "E45", {"start": v(9434.62, 0) * mm, "end": v(9239.75, 0) * mm});
            skLineSegment(sketch, "E46", {"start": v(9239.75, 190.5) * mm, "end": v(11195.55, 1524) * mm, "construction": true});
            skPoint(sketch, "E47", {"position": v(9337.18, 0) * mm});
            skLineSegment(sketch, "E48", {"start": v(9239.75, 190.5) * mm, "end": v(9239.75, 0) * mm});
            skLineSegment(sketch, "E49", {"start": v(9434.62, 0) * mm, "end": v(11930.6, 1701.8) * mm});
            skLineSegment(sketch, "E50", {"start": v(11930.6, 1701.8) * mm, "end": v(11474.95, 1701.8) * mm});
            skLineSegment(sketch, "E51", {"start": v(11474.95, 1701.8) * mm, "end": v(11474.95, 1524) * mm});
            skSolve(sketch);
        }
        {
            var Q0;
            Q0=qSketchRegion(id+"F12",true);
            var Q1;
            Q1=makeQuery(id+"F11.boolean.opBoolean","COPY",FACE,{"derivedFrom":makeQuery(id+"F11.opExtrude","SWEPT_FACE",FACE,{"disambiguationData":[OSD([sQuery(id+"F10.wireOp",EDGE,"E29.top")])]})});
            extrude(context, id + "F13", {"entities" : qUnion([Q0]), "operationType" : NewBodyOperationType.ADD, "endBound" : BoundingType.UP_TO_SURFACE, "oppositeDirection" : true, "depth" : 25.4 * mm, "endBoundEntityFace" : qUnion([Q1]), "offsetDistance" : 25.4 * mm});
        }
        {
            var Q0;
            Q0=makeQuery(id+"F9.boolean.opBoolean","MERGE",FACE,{"derivedFrom":[makeQuery(id+"F7.boolean.opBoolean","MERGE",FACE,{"derivedFrom":[makeQuery(id+"F5.boolean.opBoolean","MERGE",FACE,{"derivedFrom":[makeQuery(id+"F3.opExtrude","CAP_FACE",FACE,{"disambiguationData":[OSD([sQuery(id+"F2.wireOp",EDGE,"E8.0"),sQuery(id+"F2.wireOp",EDGE,"E9.0"),sQuery(id+"F2.wireOp",EDGE,"E9.1"),sQuery(id+"F2.wireOp",EDGE,"E10"),sQuery(id+"F2.wireOp",EDGE,"E11"),sQuery(id+"F2.wireOp",EDGE,"E12"),sQuery(id+"F2.wireOp",EDGE,"E14.0"),sQuery(id+"F2.wireOp",EDGE,"E14.1"),sQuery(id+"F2.wireOp",EDGE,"E14.2"),sQuery(id+"F2.wireOp",EDGE,"E14.3"),sQuery(id+"F2.wireOp",EDGE,"E14.4"),sQuery(id+"F2.wireOp",EDGE,"E14.5")])],"isStart":false}),makeQuery(id+"F5.opExtrude","CAP_FACE",FACE,{"disambiguationData":[OSD([sQuery(id+"F4.wireOp",EDGE,"E15.bottom"),sQuery(id+"F4.wireOp",EDGE,"E15.top"),sQuery(id+"F4.wireOp",EDGE,"E15.left"),sQuery(id+"F4.wireOp",EDGE,"E15.right")])],"isStart":false})]}),makeQuery(id+"F7.opExtrude","CAP_FACE",FACE,{"disambiguationData":[OSD([sQuery(id+"F6.wireOp",EDGE,"E16.bottom"),sQuery(id+"F6.wireOp",EDGE,"E16.top"),sQuery(id+"F6.wireOp",EDGE,"E16.left"),sQuery(id+"F6.wireOp",EDGE,"E16.right")])],"isStart":false}),makeQuery(id+"F7.opExtrude","CAP_FACE",FACE,{"disambiguationData":[OSD([sQuery(id+"F6.wireOp",EDGE,"E17.1.0.0"),sQuery(id+"F6.wireOp",EDGE,"E17.1.0.1"),sQuery(id+"F6.wireOp",EDGE,"E17.1.0.2"),sQuery(id+"F6.wireOp",EDGE,"E17.1.0.3")])],"isStart":false}),makeQuery(id+"F7.opExtrude","CAP_FACE",FACE,{"disambiguationData":[OSD([sQuery(id+"F6.wireOp",EDGE,"E17.2.0.0"),sQuery(id+"F6.wireOp",EDGE,"E17.2.0.1"),sQuery(id+"F6.wireOp",EDGE,"E17.2.0.2"),sQuery(id+"F6.wireOp",EDGE,"E17.2.0.3")])],"isStart":false}),makeQuery(id+"F7.opExtrude","CAP_FACE",FACE,{"disambiguationData":[OSD([sQuery(id+"F6.wireOp",EDGE,"E17.3.0.0"),sQuery(id+"F6.wireOp",EDGE,"E17.3.0.1"),sQuery(id+"F6.wireOp",EDGE,"E17.3.0.2"),sQuery(id+"F6.wireOp",EDGE,"E17.3.0.3")])],"isStart":false}),makeQuery(id+"F7.opExtrude","CAP_FACE",FACE,{"disambiguationData":[OSD([sQuery(id+"F6.wireOp",EDGE,"E17.4.0.0"),sQuery(id+"F6.wireOp",EDGE,"E17.4.0.1"),sQuery(id+"F6.wireOp",EDGE,"E17.4.0.2"),sQuery(id+"F6.wireOp",EDGE,"E17.4.0.3")])],"isStart":false}),makeQuery(id+"F7.opExtrude","CAP_FACE",FACE,{"disambiguationData":[OSD([sQuery(id+"F6.wireOp",EDGE,"E17.5.0.0"),sQuery(id+"F6.wireOp",EDGE,"E17.5.0.1"),sQuery(id+"F6.wireOp",EDGE,"E17.5.0.2"),sQuery(id+"F6.wireOp",EDGE,"E17.5.0.3")])],"isStart":false}),makeQuery(id+"F7.opExtrude","CAP_FACE",FACE,{"disambiguationData":[OSD([sQuery(id+"F6.wireOp",EDGE,"E17.6.0.0"),sQuery(id+"F6.wireOp",EDGE,"E17.6.0.1"),sQuery(id+"F6.wireOp",EDGE,"E17.6.0.2"),sQuery(id+"F6.wireOp",EDGE,"E17.6.0.3")])],"isStart":false}),makeQuery(id+"F7.opExtrude","CAP_FACE",FACE,{"disambiguationData":[OSD([sQuery(id+"F6.wireOp",EDGE,"E17.7.0.0"),sQuery(id+"F6.wireOp",EDGE,"E17.7.0.1"),sQuery(id+"F6.wireOp",EDGE,"E17.7.0.2"),sQuery(id+"F6.wireOp",EDGE,"E17.7.0.3")])],"isStart":false}),makeQuery(id+"F7.opExtrude","CAP_FACE",FACE,{"disambiguationData":[OSD([sQuery(id+"F6.wireOp",EDGE,"E17.8.0.0"),sQuery(id+"F6.wireOp",EDGE,"E17.8.0.1"),sQuery(id+"F6.wireOp",EDGE,"E17.8.0.2"),sQuery(id+"F6.wireOp",EDGE,"E17.8.0.3")])],"isStart":false}),makeQuery(id+"F7.opExtrude","CAP_FACE",FACE,{"disambiguationData":[OSD([sQuery(id+"F6.wireOp",EDGE,"E17.9.0.0"),sQuery(id+"F6.wireOp",EDGE,"E17.9.0.1"),sQuery(id+"F6.wireOp",EDGE,"E17.9.0.2"),sQuery(id+"F6.wireOp",EDGE,"E17.9.0.3")])],"isStart":false}),makeQuery(id+"F7.opExtrude","CAP_FACE",FACE,{"disambiguationData":[OSD([sQuery(id+"F6.wireOp",EDGE,"E18.top"),sQuery(id+"F6.wireOp",EDGE,"E18.left"),sQuery(id+"F6.wireOp",EDGE,"E18.right"),sQuery(id+"F6.wireOp",EDGE,"E20")])],"isStart":false}),makeQuery(id+"F7.opExtrude","CAP_FACE",FACE,{"disambiguationData":[OSD([sQuery(id+"F6.wireOp",EDGE,"E19.top"),sQuery(id+"F6.wireOp",EDGE,"E19.left"),sQuery(id+"F6.wireOp",EDGE,"E19.right"),sQuery(id+"F6.wireOp",EDGE,"E21.trimOffspring")])],"isStart":false})]}),makeQuery(id+"F9.opExtrude","CAP_FACE",FACE,{"disambiguationData":[OSD([sQuery(id+"F8.wireOp",EDGE,"E22"),sQuery(id+"F8.wireOp",EDGE,"E23"),sQuery(id+"F8.wireOp",EDGE,"E24"),sQuery(id+"F8.wireOp",EDGE,"E25"),sQuery(id+"F8.wireOp",EDGE,"E26"),sQuery(id+"F8.wireOp",EDGE,"E27"),sQuery(id+"F8.wireOp",EDGE,"E28")])],"isStart":true})]});
            var sketch = newSketch(context, id + "F14", { "sketchPlane" : qUnion([Q0])});
            skLineSegment(sketch, "E52.bottom", {"start": v(9239.75, -3042.15) * mm, "end": v(8630.15, -3042.15) * mm});
            skLineSegment(sketch, "E52.top", {"start": v(9239.75, -2026.15) * mm, "end": v(8630.15, -2026.15) * mm});
            skLineSegment(sketch, "E52.left", {"start": v(9239.75, -3042.15) * mm, "end": v(9239.75, -2026.15) * mm});
            skLineSegment(sketch, "E53", {"start": v(8630.15, -2026.15) * mm, "end": v(7614.15, -3042.15) * mm});
            skLineSegment(sketch, "E54", {"start": v(7614.15, -3042.15) * mm, "end": v(8630.15, -3042.15) * mm});
            skSolve(sketch);
        }
        {
            var Q0;
            Q0 = qSketchRegion(id + "F14", true);
            extrude(context, id + "F15", {"entities" : qUnion([Q0]), "operationType" : NewBodyOperationType.REMOVE, "endBound" : BoundingType.UP_TO_NEXT, "oppositeDirection" : true, "depth" : 25.4 * mm, "offsetDistance" : 25.4 * mm});
        }
    });
